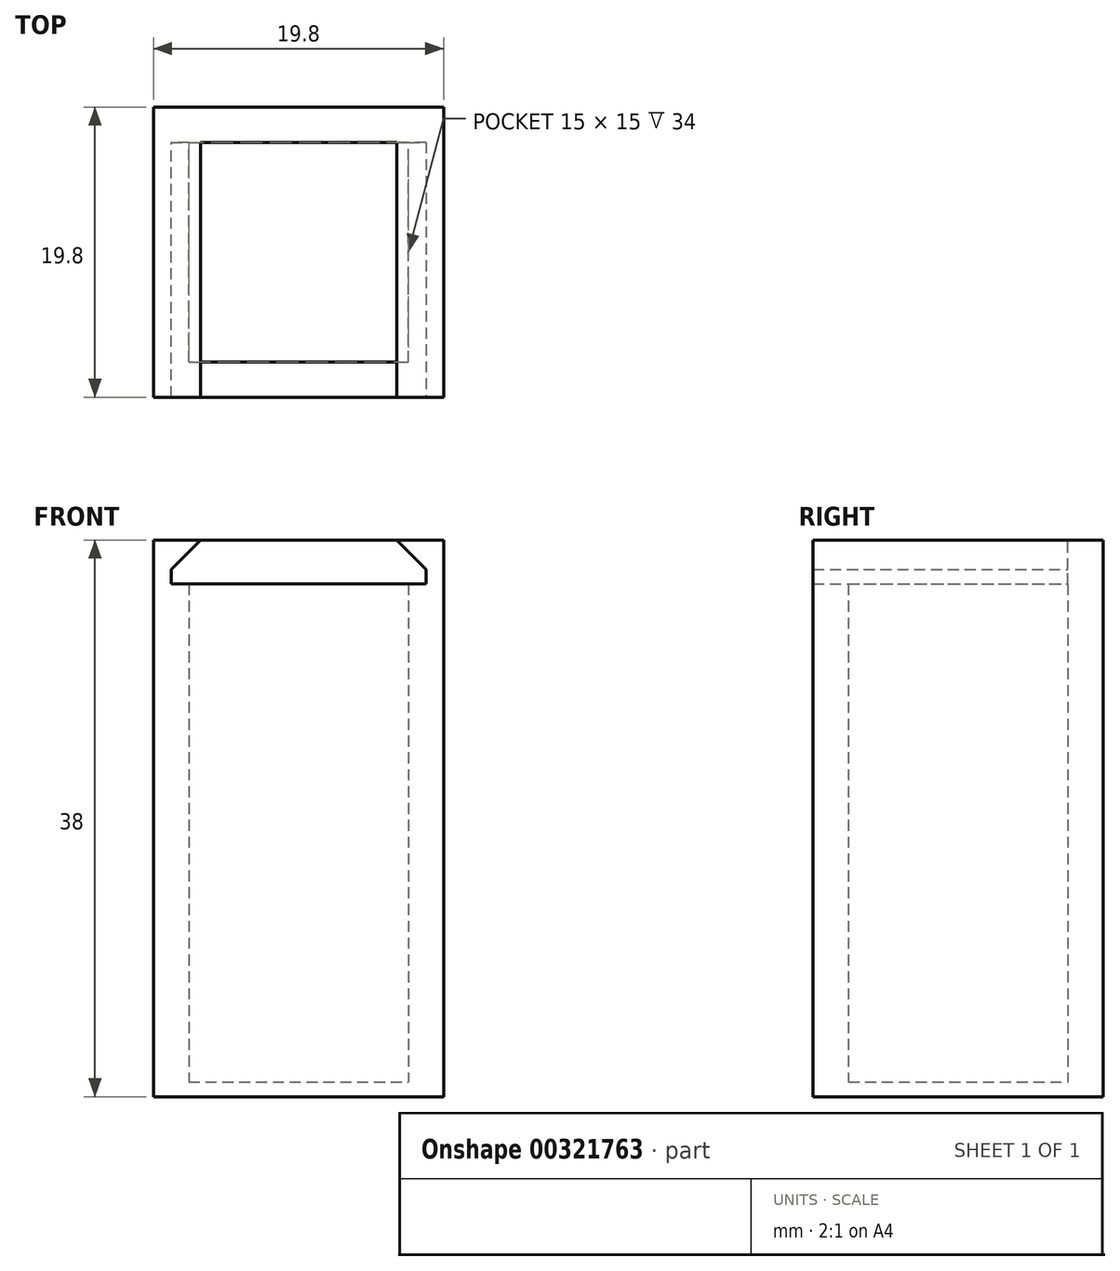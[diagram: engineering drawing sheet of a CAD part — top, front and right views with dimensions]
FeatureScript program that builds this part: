
annotation { "Feature Type Name" : "Feature", "Feature Type Description" : "" }
export const myFeature = defineFeature(function(context is Context, id is Id, definition is map)
    precondition{}
    {
        {
            var Q0;
            Q0=qCreatedBy(makeId("Top.planeOp"),FACE);
            var sketch = newSketch(context, id + "F0", { "sketchPlane" : qUnion([Q0])});
            skLineSegment(sketch, "E0.bottom", {"start": v(-7.5, -7.5) * mm, "end": v(7.5, -7.5) * mm});
            skLineSegment(sketch, "E0.top", {"start": v(-7.5, 7.5) * mm, "end": v(7.5, 7.5) * mm});
            skLineSegment(sketch, "E0.left", {"start": v(-7.5, -7.5) * mm, "end": v(-7.5, 7.5) * mm});
            skLineSegment(sketch, "E0.right", {"start": v(7.5, -7.5) * mm, "end": v(7.5, 7.5) * mm});
            skLineSegment(sketch, "E1", {"start": v(-7.5, 7.5) * mm, "end": v(-7.5, 9.9) * mm});
            skLineSegment(sketch, "E2", {"start": v(-7.5, 9.9) * mm, "end": v(-9.9, 9.9) * mm});
            skLineSegment(sketch, "E3", {"start": v(7.5, -7.5) * mm, "end": v(9.9, -7.5) * mm});
            skLineSegment(sketch, "E4", {"start": v(9.9, -7.5) * mm, "end": v(9.9, -9.9) * mm});
            skLineSegment(sketch, "E5", {"start": v(-7.5, 0) * mm, "end": v(0, 0) * mm});
            skLineSegment(sketch, "E6", {"start": v(0, 0) * mm, "end": v(0, -7.5) * mm});
            skLineSegment(sketch, "E7.bottom", {"start": v(-9.9, 9.9) * mm, "end": v(9.9, 9.9) * mm});
            skLineSegment(sketch, "E7.top", {"start": v(-9.9, -9.9) * mm, "end": v(9.9, -9.9) * mm});
            skLineSegment(sketch, "E7.left", {"start": v(-9.9, 9.9) * mm, "end": v(-9.9, -9.9) * mm});
            skLineSegment(sketch, "E7.right", {"start": v(9.9, 9.9) * mm, "end": v(9.9, -9.9) * mm});
            skSolve(sketch);
        }
        {
            var Q0;
            {var subQ0=sQuery(id+"F0.wireOp",EDGE,"E1");Q0=makeQuery(id+"F0.imprint","IMPRINT",FACE,{"disambiguationData":[TD([[makeQuery(id+"F0.imprint","IMPRINT",EDGE,{"derivedFrom":subQ0}),1.0]])]});}
            var Q1;
            Q1=makeQuery(id+"F0.imprint","IMPRINT",FACE,{"disambiguationData":[TD([[makeQuery(id+"F0.imprint","IMPRINT",EDGE,{"derivedFrom":sQuery(id+"F0.wireOp",EDGE,"E0.top")}),1.0]])]});
            extrude(context, id + "F1", {"entities" : qUnion([Q0, Q1]), "depth" : 25 * mm});
        }
        {
            var Q0;
            Q0=makeQuery(id+"F1.opExtrude","CAP_FACE",FACE,{"disambiguationData":[OSD([sQuery(id+"F0.wireOp",EDGE,"E0.bottom"),sQuery(id+"F0.wireOp",EDGE,"E0.top"),sQuery(id+"F0.wireOp",EDGE,"E0.left"),sQuery(id+"F0.wireOp",EDGE,"E0.right"),sQuery(id+"F0.wireOp",EDGE,"E7.bottom"),sQuery(id+"F0.wireOp",EDGE,"E7.top"),sQuery(id+"F0.wireOp",EDGE,"E7.left"),sQuery(id+"F0.wireOp",EDGE,"E7.right")])],"isStart":true});
            var sketch = newSketch(context, id + "F2", { "sketchPlane" : qUnion([Q0])});
            skLineSegment(sketch, "E8.bottom", {"start": v(-9.9, 9.9) * mm, "end": v(9.9, 9.9) * mm});
            skLineSegment(sketch, "E8.top", {"start": v(-9.9, -9.9) * mm, "end": v(9.9, -9.9) * mm});
            skLineSegment(sketch, "E8.left", {"start": v(-9.9, 9.9) * mm, "end": v(-9.9, -9.9) * mm});
            skLineSegment(sketch, "E8.right", {"start": v(9.9, 9.9) * mm, "end": v(9.9, -9.9) * mm});
            skSolve(sketch);
        }
        {
            var Q0;
            Q0=qSketchRegion(id+"F2",true);
            extrude(context, id + "F3", {"entities" : qUnion([Q0]), "operationType" : NewBodyOperationType.ADD, "depth" : 1 * mm});
        }
        {
            var Q0;
            Q0=makeQuery(id+"F1.opExtrude","CAP_FACE",FACE,{"disambiguationData":[OSD([sQuery(id+"F0.wireOp",EDGE,"E0.bottom"),sQuery(id+"F0.wireOp",EDGE,"E0.top"),sQuery(id+"F0.wireOp",EDGE,"E0.left"),sQuery(id+"F0.wireOp",EDGE,"E0.right"),sQuery(id+"F0.wireOp",EDGE,"E7.bottom"),sQuery(id+"F0.wireOp",EDGE,"E7.top"),sQuery(id+"F0.wireOp",EDGE,"E7.left"),sQuery(id+"F0.wireOp",EDGE,"E7.right")])],"isStart":false});
            var sketch = newSketch(context, id + "F4", { "sketchPlane" : qUnion([Q0])});
            skLineSegment(sketch, "E9", {"start": v(-9.9, 0) * mm, "end": v(-8.7, 0) * mm});
            skPoint(sketch, "E9.endSnap0", {"position": v(-7.5, 0) * mm});
            skLineSegment(sketch, "E10", {"start": v(9.9, 0) * mm, "end": v(8.7, 0) * mm});
            skLineSegment(sketch, "E11", {"start": v(-8.7, 0) * mm, "end": v(-8.7, -10.6) * mm});
            skLineSegment(sketch, "E12", {"start": v(8.7, 0) * mm, "end": v(8.7, -11.22) * mm});
            skLineSegment(sketch, "E13", {"start": v(-8.7, -10.6) * mm, "end": v(8.7, -10.6) * mm});
            skLineSegment(sketch, "E14", {"start": v(-7.5, 7.5) * mm, "end": v(-9.9, 7.5) * mm});
            skLineSegment(sketch, "E15", {"start": v(7.5, 7.5) * mm, "end": v(9.9, 7.5) * mm});
            skLineSegment(sketch, "E16", {"start": v(-8.7, 0) * mm, "end": v(-8.7, 7.5) * mm});
            skLineSegment(sketch, "E17", {"start": v(8.7, 0) * mm, "end": v(8.7, 7.5) * mm});
            skLineSegment(sketch, "E18", {"start": v(-7.5, 7.5) * mm, "end": v(7.5, 7.5) * mm});
            skSolve(sketch);
        }
        {
            var Q0;
            {var subQ11=sQuery(id+"F4.wireOp",EDGE,"E16");Q0=makeQuery(id+"F4.imprint","IMPRINT",FACE,{"disambiguationData":[TD([[makeQuery(id+"F4.imprint","IMPRINT",EDGE,{"derivedFrom":subQ11}),-1.0]])]});}
            extrude(context, id + "F5", {"entities" : qUnion([Q0]), "operationType" : NewBodyOperationType.REMOVE, "oppositeDirection" : true, "depth" : 2 * mm});
        }
        {
            var Q0;
            Q0=makeQuery(id+"F3.boolean.opBoolean","MERGE",FACE,{"derivedFrom":[makeQuery(id+"F1.opExtrude","SWEPT_FACE",FACE,{"disambiguationData":[OSD([sQuery(id+"F0.wireOp",EDGE,"E7.top")])]}),makeQuery(id+"F3.opExtrude","SWEPT_FACE",FACE,{"disambiguationData":[OSD([sQuery(id+"F2.wireOp",EDGE,"E8.bottom")])]})]});
            var sketch = newSketch(context, id + "F6", { "sketchPlane" : qUnion([Q0])});
            skLineSegment(sketch, "E19", {"start": v(-9.9, 25) * mm, "end": v(-9.9, 27) * mm});
            skLineSegment(sketch, "E20", {"start": v(9.9, 25) * mm, "end": v(9.9, 27) * mm});
            skLineSegment(sketch, "E21", {"start": v(-9.9, 27) * mm, "end": v(9.9, 27) * mm});
            skLineSegment(sketch, "E22", {"start": v(-8.7, 25) * mm, "end": v(-6.7, 27) * mm});
            skLineSegment(sketch, "E23", {"start": v(8.7, 25) * mm, "end": v(6.7, 27) * mm});
            skLineSegment(sketch, "E24", {"start": v(-9.9, 25) * mm, "end": v(-8.7, 25) * mm});
            skLineSegment(sketch, "E25", {"start": v(8.7, 25) * mm, "end": v(9.9, 25) * mm});
            skSolve(sketch);
        }
        {
            var Q0;
            Q0=makeQuery(id+"F5.boolean.opBoolean","COPY",FACE,{"derivedFrom":makeQuery(id+"F5.opExtrude","CAP_FACE",FACE,{"disambiguationData":[OSD([sQuery(id+"F0.wireOp",EDGE,"E0.bottom"),sQuery(id+"F0.wireOp",EDGE,"E0.left"),sQuery(id+"F0.wireOp",EDGE,"E0.right"),sQuery(id+"F0.wireOp",EDGE,"E7.top"),sQuery(id+"F4.wireOp",EDGE,"E11"),sQuery(id+"F4.wireOp",EDGE,"E12"),sQuery(id+"F4.wireOp",EDGE,"E14"),sQuery(id+"F4.wireOp",EDGE,"E15"),sQuery(id+"F4.wireOp",EDGE,"E16"),sQuery(id+"F4.wireOp",EDGE,"E17")])],"isStart":false})});
            extrude(context, id + "F7", {"entities" : qUnion([Q0]), "operationType" : NewBodyOperationType.ADD, "depth" : 1 * mm});
        }
        {
            var Q0;
            {var subQ0=sQuery(id+"F6.wireOp",EDGE,"E19");Q0=makeQuery(id+"F6.imprint","IMPRINT",FACE,{"disambiguationData":[TD([[makeQuery(id+"F6.imprint","IMPRINT",EDGE,{"derivedFrom":subQ0}),-1.0]])]});}
            var Q1;
            {var subQ0=sQuery(id+"F6.wireOp",EDGE,"E20");Q1=makeQuery(id+"F6.imprint","IMPRINT",FACE,{"disambiguationData":[TD([[makeQuery(id+"F6.imprint","IMPRINT",EDGE,{"derivedFrom":subQ0}),1.0]])]});}
            var Q2;
            Q2=makeQuery(id+"F3.boolean.opBoolean","MERGE",FACE,{"derivedFrom":[makeQuery(id+"F1.opExtrude","SWEPT_FACE",FACE,{"disambiguationData":[OSD([sQuery(id+"F0.wireOp",EDGE,"E7.bottom")])]}),makeQuery(id+"F3.opExtrude","SWEPT_FACE",FACE,{"disambiguationData":[OSD([sQuery(id+"F2.wireOp",EDGE,"E8.top")])]})]});
            extrude(context, id + "F8", {"entities" : qUnion([Q0, Q1]), "operationType" : NewBodyOperationType.ADD, "endBound" : BoundingType.UP_TO_SURFACE, "oppositeDirection" : true, "endBoundEntityFace" : qUnion([Q2]), "depth" : 25 * mm});
        }
        {
            var Q0;
            {var subQ0=sQuery(id+"F6.wireOp",EDGE,"E21");var subQ1=sQuery(id+"F2.wireOp",EDGE,"E8.top");var subQ2=sQuery(id+"F0.wireOp",EDGE,"E7.bottom");Q0=makeQuery(id+"F8.boolean.opBoolean","MERGE",FACE,{"derivedFrom":[makeQuery(id+"F3.boolean.opBoolean","MERGE",FACE,{"derivedFrom":[makeQuery(id+"F1.opExtrude","SWEPT_FACE",FACE,{"disambiguationData":[OSD([subQ2])]}),makeQuery(id+"F3.opExtrude","SWEPT_FACE",FACE,{"disambiguationData":[OSD([subQ1])]})]}),makeQuery(id+"F8.opExtrude","CAP_FACE",FACE,{"disambiguationData":[OSD([subQ2,subQ1]),ownerDisambiguation([makeQuery(id+"F8.opExtrude","SWEPT_BODY",BODY,{"disambiguationData":[OSD([sQuery(id+"F6.wireOp",EDGE,"E19"),subQ0,sQuery(id+"F6.wireOp",EDGE,"E22"),sQuery(id+"F6.wireOp",EDGE,"E24")])]})])],"isStart":false}),makeQuery(id+"F8.opExtrude","CAP_FACE",FACE,{"disambiguationData":[OSD([subQ2,subQ1]),ownerDisambiguation([makeQuery(id+"F8.opExtrude","SWEPT_BODY",BODY,{"disambiguationData":[OSD([sQuery(id+"F6.wireOp",EDGE,"E20"),subQ0,sQuery(id+"F6.wireOp",EDGE,"E23"),sQuery(id+"F6.wireOp",EDGE,"E25")])]})])],"isStart":false})]});}
            var sketch = newSketch(context, id + "F9", { "sketchPlane" : qUnion([Q0])});
            skLineSegment(sketch, "E26", {"start": v(-6.7, 27) * mm, "end": v(-6.7, 25) * mm});
            skLineSegment(sketch, "E27", {"start": v(-6.7, 25) * mm, "end": v(-8.7, 25) * mm});
            skLineSegment(sketch, "E28", {"start": v(-8.7, 25) * mm, "end": v(-6.7, 27) * mm});
            skLineSegment(sketch, "E29", {"start": v(6.7, 27) * mm, "end": v(6.7, 25) * mm});
            skLineSegment(sketch, "E30", {"start": v(6.7, 25) * mm, "end": v(8.7, 25) * mm});
            skLineSegment(sketch, "E31", {"start": v(8.7, 25) * mm, "end": v(6.7, 27) * mm});
            skSolve(sketch);
        }
        {
            var Q0;
            Q0=makeQuery(id+"F9.imprint","IMPRINT",FACE,{"disambiguationData":[TD([[makeQuery(id+"F9.imprint","IMPRINT",EDGE,{"derivedFrom":sQuery(id+"F9.wireOp",EDGE,"E26")}),-1.0]])]});
            var Q1;
            Q1=makeQuery(id+"F9.imprint","IMPRINT",FACE,{"disambiguationData":[TD([[makeQuery(id+"F9.imprint","IMPRINT",EDGE,{"derivedFrom":sQuery(id+"F9.wireOp",EDGE,"E29")}),1.0]])]});
            var Q2;
            Q2=makeQuery(id+"F5.boolean.opBoolean","MERGE",FACE,{"derivedFrom":[makeQuery(id+"F1.opExtrude","SWEPT_FACE",FACE,{"disambiguationData":[OSD([sQuery(id+"F0.wireOp",EDGE,"E0.top")])]}),makeQuery(id+"F5.opExtrude","SWEPT_FACE",FACE,{"disambiguationData":[OSD([sQuery(id+"F4.wireOp",EDGE,"E14")])]}),makeQuery(id+"F5.opExtrude","SWEPT_FACE",FACE,{"disambiguationData":[OSD([sQuery(id+"F4.wireOp",EDGE,"E15")])]})]});
            extrude(context, id + "F10", {"entities" : qUnion([Q0, Q1]), "operationType" : NewBodyOperationType.ADD, "endBound" : BoundingType.UP_TO_SURFACE, "oppositeDirection" : true, "endBoundEntityFace" : qUnion([Q2]), "depth" : 25 * mm});
        }
        {
            var Q0;
            Q0=makeQuery(id+"F1.opExtrude","CAP_FACE",FACE,{"disambiguationData":[OSD([sQuery(id+"F0.wireOp",EDGE,"E0.bottom"),sQuery(id+"F0.wireOp",EDGE,"E0.top"),sQuery(id+"F0.wireOp",EDGE,"E0.left"),sQuery(id+"F0.wireOp",EDGE,"E0.right"),sQuery(id+"F0.wireOp",EDGE,"E7.bottom"),sQuery(id+"F0.wireOp",EDGE,"E7.top"),sQuery(id+"F0.wireOp",EDGE,"E7.left"),sQuery(id+"F0.wireOp",EDGE,"E7.right")])],"isStart":false});
            var Q1;
            {var subQ0=sQuery(id+"F6.wireOp",EDGE,"E21");Q1=makeQuery(id+"F8.opExtrude","SWEPT_FACE",FACE,{"disambiguationData":[OSD([subQ0]),TDD([makeQuery(id+"F6.imprint","IMPRINT",EDGE,{"disambiguationData":[TD([[makeQuery(id+"F6.imprint","INTERSECT",VERTEX,{"derivedFrom":[sQuery(id+"F6.wireOp",EDGE,"E20"),subQ0]}),1.0]])],"derivedFrom":subQ0})])]});}
            extrude(context, id + "F11", {"entities" : qUnion([Q0]), "operationType" : NewBodyOperationType.ADD, "endBound" : BoundingType.UP_TO_SURFACE, "endBoundEntityFace" : qUnion([Q1]), "depth" : 25 * mm});
        }
        {
            var Q0;
            {var subQ0=sQuery(id+"F6.wireOp",EDGE,"E21");var subQ1=sQuery(id+"F0.wireOp",EDGE,"E7.top");Q0=makeQuery(id+"F8.boolean.opBoolean","MERGE",FACE,{"derivedFrom":[makeQuery(id+"F7.boolean.opBoolean","MERGE",FACE,{"derivedFrom":[makeQuery(id+"F3.boolean.opBoolean","MERGE",FACE,{"derivedFrom":[makeQuery(id+"F1.opExtrude","SWEPT_FACE",FACE,{"disambiguationData":[OSD([subQ1])]}),makeQuery(id+"F3.opExtrude","SWEPT_FACE",FACE,{"disambiguationData":[OSD([sQuery(id+"F2.wireOp",EDGE,"E8.bottom")])]})]}),makeQuery(id+"F7.opExtrude","SWEPT_FACE",FACE,{"disambiguationData":[OSD([subQ1])]})]}),makeQuery(id+"F8.opExtrude","CAP_FACE",FACE,{"disambiguationData":[OSD([sQuery(id+"F6.wireOp",EDGE,"E19"),subQ0,sQuery(id+"F6.wireOp",EDGE,"E22"),sQuery(id+"F6.wireOp",EDGE,"E24")])],"isStart":true}),makeQuery(id+"F8.opExtrude","CAP_FACE",FACE,{"disambiguationData":[OSD([sQuery(id+"F6.wireOp",EDGE,"E20"),subQ0,sQuery(id+"F6.wireOp",EDGE,"E23"),sQuery(id+"F6.wireOp",EDGE,"E25")])],"isStart":true})]});}
            var sketch = newSketch(context, id + "F12", { "sketchPlane" : qUnion([Q0])});
            skLineSegment(sketch, "E32.0", {"start": v(-8.6, 24.1) * mm, "end": v(-8.6, 24.96) * mm});
            skLineSegment(sketch, "E33.0", {"start": v(-8.6, 24.96) * mm, "end": v(-6.63, 26.93) * mm});
            skLineSegment(sketch, "E34.0", {"start": v(-8.6, 24.1) * mm, "end": v(8.6, 24.1) * mm});
            skLineSegment(sketch, "E35.0", {"start": v(8.6, 24.1) * mm, "end": v(8.6, 24.96) * mm});
            skLineSegment(sketch, "E36.0", {"start": v(8.6, 24.96) * mm, "end": v(6.63, 26.93) * mm});
            skLineSegment(sketch, "E37", {"start": v(-6.63, 26.93) * mm, "end": v(6.63, 26.93) * mm});
            skSolve(sketch);
        }
        {
            var Q0;
            Q0=makeQuery(id+"F12.imprint","IMPRINT",FACE,{"disambiguationData":[TD([[makeQuery(id+"F12.imprint","IMPRINT",EDGE,{"derivedFrom":sQuery(id+"F12.wireOp",EDGE,"E32.0")}),-1.0]])]});
            var Q1;
            {var subQ0=sQuery(id+"F4.wireOp",EDGE,"E15");var subQ1=sQuery(id+"F4.wireOp",EDGE,"E14");var subQ2=sQuery(id+"F0.wireOp",EDGE,"E0.top");Q1=makeQuery(id+"F11.boolean.opBoolean","MERGE",FACE,{"derivedFrom":[makeQuery(id+"F10.boolean.opBoolean","MERGE",FACE,{"derivedFrom":[makeQuery(id+"F5.boolean.opBoolean","MERGE",FACE,{"derivedFrom":[makeQuery(id+"F1.opExtrude","SWEPT_FACE",FACE,{"disambiguationData":[OSD([subQ2])]}),makeQuery(id+"F5.opExtrude","SWEPT_FACE",FACE,{"disambiguationData":[OSD([subQ1])]}),makeQuery(id+"F5.opExtrude","SWEPT_FACE",FACE,{"disambiguationData":[OSD([subQ0])]})]}),makeQuery(id+"F10.opExtrude","CAP_FACE",FACE,{"disambiguationData":[OSD([subQ2,subQ1,subQ0]),ownerDisambiguation([makeQuery(id+"F10.opExtrude","SWEPT_BODY",BODY,{"disambiguationData":[OSD([sQuery(id+"F9.wireOp",EDGE,"E26"),sQuery(id+"F9.wireOp",EDGE,"E27"),sQuery(id+"F9.wireOp",EDGE,"E28")])]})])],"isStart":false}),makeQuery(id+"F10.opExtrude","CAP_FACE",FACE,{"disambiguationData":[OSD([subQ2,subQ1,subQ0]),ownerDisambiguation([makeQuery(id+"F10.opExtrude","SWEPT_BODY",BODY,{"disambiguationData":[OSD([sQuery(id+"F9.wireOp",EDGE,"E29"),sQuery(id+"F9.wireOp",EDGE,"E30"),sQuery(id+"F9.wireOp",EDGE,"E31")])]})])],"isStart":false})]}),makeQuery(id+"F11.opExtrude","SWEPT_FACE",FACE,{"disambiguationData":[OSD([subQ2,subQ1,subQ0])]})]});}
            extrude(context, id + "F13", {"entities" : qUnion([Q0]), "endBound" : BoundingType.UP_TO_SURFACE, "oppositeDirection" : true, "endBoundEntityFace" : qUnion([Q1]), "depth" : 25 * mm});
        }
        {
            var Q0;
            Q0=makeQuery(id+"F13.opExtrude","SWEPT_FACE",FACE,{"disambiguationData":[OSD([sQuery(id+"F12.wireOp",EDGE,"E37")])]});
            var sketch = newSketch(context, id + "F14", { "sketchPlane" : qUnion([Q0])});
            skText(sketch, "E38", { "text": "0.4", "fontName": "OpenSans-Regular.ttf"});
            const initialGuessF14  = {"E38": [-0.00317, 0.00541, 0, -1, 0.00637]};
            skSetInitialGuess(sketch, initialGuessF14);
            skSolve(sketch);
        }
        {
            var Q0;
            Q0=qSketchRegion(id+"F14",true);
            extrude(context, id + "F15", {"entities" : qUnion([Q0]), "operationType" : NewBodyOperationType.REMOVE, "oppositeDirection" : true, "depth" : 2 * mm});
        }
        {
            var Q0;
            Q0=makeQuery(id+"F15.boolean.opBoolean","COPY",FACE,{"derivedFrom":makeQuery(id+"F15.opExtrude","CAP_FACE",FACE,{"disambiguationData":[OSD([sQuery(id+"F14.wireOp",EDGE,"E38.sketch_text.stroke-0"),sQuery(id+"F14.wireOp",EDGE,"E38.sketch_text.stroke-1"),sQuery(id+"F14.wireOp",EDGE,"E38.sketch_text.stroke-2"),sQuery(id+"F14.wireOp",EDGE,"E38.sketch_text.stroke-3"),sQuery(id+"F14.wireOp",EDGE,"E38.sketch_text.stroke-4"),sQuery(id+"F14.wireOp",EDGE,"E38.sketch_text.stroke-5"),sQuery(id+"F14.wireOp",EDGE,"E38.sketch_text.stroke-6"),sQuery(id+"F14.wireOp",EDGE,"E38.sketch_text.stroke-7"),sQuery(id+"F14.wireOp",EDGE,"E38.sketch_text.stroke-8"),sQuery(id+"F14.wireOp",EDGE,"E38.sketch_text.stroke-9"),sQuery(id+"F14.wireOp",EDGE,"E38.sketch_text.stroke-10"),sQuery(id+"F14.wireOp",EDGE,"E38.sketch_text.stroke-11"),sQuery(id+"F14.wireOp",EDGE,"E38.sketch_text.stroke-12"),sQuery(id+"F14.wireOp",EDGE,"E38.sketch_text.stroke-13"),sQuery(id+"F14.wireOp",EDGE,"E38.sketch_text.stroke-14"),sQuery(id+"F14.wireOp",EDGE,"E38.sketch_text.stroke-15")])],"isStart":false})});
            var Q1;
            Q1=makeQuery(id+"F15.boolean.opBoolean","COPY",FACE,{"derivedFrom":makeQuery(id+"F15.opExtrude","CAP_FACE",FACE,{"disambiguationData":[OSD([sQuery(id+"F14.wireOp",EDGE,"E38.sketch_text.stroke-16"),sQuery(id+"F14.wireOp",EDGE,"E38.sketch_text.stroke-17"),sQuery(id+"F14.wireOp",EDGE,"E38.sketch_text.stroke-18"),sQuery(id+"F14.wireOp",EDGE,"E38.sketch_text.stroke-19"),sQuery(id+"F14.wireOp",EDGE,"E38.sketch_text.stroke-20"),sQuery(id+"F14.wireOp",EDGE,"E38.sketch_text.stroke-21"),sQuery(id+"F14.wireOp",EDGE,"E38.sketch_text.stroke-22"),sQuery(id+"F14.wireOp",EDGE,"E38.sketch_text.stroke-23")])],"isStart":false})});
            var Q2;
            Q2=makeQuery(id+"F15.boolean.opBoolean","COPY",FACE,{"derivedFrom":makeQuery(id+"F15.opExtrude","CAP_FACE",FACE,{"disambiguationData":[OSD([sQuery(id+"F14.wireOp",EDGE,"E38.sketch_text.stroke-24"),sQuery(id+"F14.wireOp",EDGE,"E38.sketch_text.stroke-25"),sQuery(id+"F14.wireOp",EDGE,"E38.sketch_text.stroke-26"),sQuery(id+"F14.wireOp",EDGE,"E38.sketch_text.stroke-27"),sQuery(id+"F14.wireOp",EDGE,"E38.sketch_text.stroke-28"),sQuery(id+"F14.wireOp",EDGE,"E38.sketch_text.stroke-29"),sQuery(id+"F14.wireOp",EDGE,"E38.sketch_text.stroke-30"),sQuery(id+"F14.wireOp",EDGE,"E38.sketch_text.stroke-31"),sQuery(id+"F14.wireOp",EDGE,"E38.sketch_text.stroke-32"),sQuery(id+"F14.wireOp",EDGE,"E38.sketch_text.stroke-33"),sQuery(id+"F14.wireOp",EDGE,"E38.sketch_text.stroke-34"),sQuery(id+"F14.wireOp",EDGE,"E38.sketch_text.stroke-35"),sQuery(id+"F14.wireOp",EDGE,"E38.sketch_text.stroke-36"),sQuery(id+"F14.wireOp",EDGE,"E38.sketch_text.stroke-37"),sQuery(id+"F14.wireOp",EDGE,"E38.sketch_text.stroke-38"),sQuery(id+"F14.wireOp",EDGE,"E38.sketch_text.stroke-39"),sQuery(id+"F14.wireOp",EDGE,"E38.sketch_text.stroke-40")])],"isStart":false})});
            extrude(context, id + "F16", {"entities" : qUnion([Q0, Q1, Q2]), "operationType" : NewBodyOperationType.REMOVE, "oppositeDirection" : true, "depth" : 2 * mm});
        }
        {
            var Q0;
            {var subQ1=sQuery(id+"F12.wireOp",EDGE,"E33.0");var subQ2=sQuery(id+"F12.wireOp",EDGE,"E37");Q0=makeQuery(id+"F15.boolean.opBoolean","SPLIT",FACE,{"disambiguationData":[TD([makeQuery(id+"F13.opExtrude","SWEPT_FACE",FACE,{"disambiguationData":[OSD([subQ1])]})])],"derivedFrom":makeQuery(id+"F13.opExtrude","SWEPT_FACE",FACE,{"disambiguationData":[OSD([subQ2])]})});}
            var sketch = newSketch(context, id + "F17", { "sketchPlane" : qUnion([Q0])});
            skLineSegment(sketch, "E39", {"start": v(0, 4.97) * mm, "end": v(0, 4) * mm});
            skLineSegment(sketch, "E40", {"start": v(0, 4) * mm, "end": v(-0.49, 4) * mm});
            skLineSegment(sketch, "E41", {"start": v(-0.49, 4) * mm, "end": v(-0.49, 5.29) * mm});
            skLineSegment(sketch, "E42", {"start": v(-0.49, 5.29) * mm, "end": v(0.54, 5.29) * mm});
            skLineSegment(sketch, "E43", {"start": v(0.54, 5.29) * mm, "end": v(0.54, 4) * mm});
            skLineSegment(sketch, "E44", {"start": v(0.54, 4) * mm, "end": v(0, 4) * mm});
            skLineSegment(sketch, "E45", {"start": v(-0.49, 1.88) * mm, "end": v(0.43, 1.88) * mm});
            skLineSegment(sketch, "E46", {"start": v(0.43, 1.88) * mm, "end": v(0.43, 0.38) * mm});
            skLineSegment(sketch, "E47", {"start": v(0.43, 0.38) * mm, "end": v(-0.49, 0.38) * mm});
            skLineSegment(sketch, "E48", {"start": v(-0.49, 0.38) * mm, "end": v(-0.49, 1.88) * mm});
            skLineSegment(sketch, "E49", {"start": v(-1.72, -5.25) * mm, "end": v(-0.8, -5.25) * mm});
            skLineSegment(sketch, "E50", {"start": v(-0.8, -5.25) * mm, "end": v(-0.8, -4.57) * mm});
            skLineSegment(sketch, "E51", {"start": v(-0.8, -4.57) * mm, "end": v(-2.2, -4.57) * mm});
            skLineSegment(sketch, "E52", {"start": v(-2.2, -4.57) * mm, "end": v(-1.72, -5.25) * mm});
            skSolve(sketch);
        }
        {
            var Q0;
            {var subQ0=sQuery(id+"F17.wireOp",EDGE,"E39");Q0=makeQuery(id+"F17.imprint","IMPRINT",FACE,{"disambiguationData":[TD([[makeQuery(id+"F17.imprint","IMPRINT",EDGE,{"derivedFrom":subQ0}),-1.0]])]});}
            var Q1;
            {var subQ0=sQuery(id+"F17.wireOp",EDGE,"E39");Q1=makeQuery(id+"F17.imprint","IMPRINT",FACE,{"disambiguationData":[TD([[makeQuery(id+"F17.imprint","IMPRINT",EDGE,{"derivedFrom":subQ0}),1.0]])]});}
            var Q2;
            {var subQ6=sQuery(id+"F17.wireOp",EDGE,"E45");Q2=makeQuery(id+"F17.imprint","IMPRINT",FACE,{"disambiguationData":[TD([[makeQuery(id+"F17.imprint","IMPRINT",EDGE,{"derivedFrom":subQ6}),-1.0]])]});}
            var Q3;
            {var subQ0=sQuery(id+"F17.wireOp",EDGE,"E49");Q3=makeQuery(id+"F17.imprint","IMPRINT",FACE,{"disambiguationData":[TD([[makeQuery(id+"F17.imprint","IMPRINT",EDGE,{"derivedFrom":subQ0}),1.0]])]});}
            var Q4;
            {var subQ27=sQuery(id+"F12.wireOp",EDGE,"E32.0");var subQ29=sQuery(id+"F12.wireOp",EDGE,"E34.0");Q4=makeQuery(id+"F16.boolean.opBoolean","SPLIT",FACE,{"disambiguationData":[TD([makeQuery(id+"F13.opExtrude","SWEPT_FACE",FACE,{"disambiguationData":[OSD([subQ27])]})])],"derivedFrom":makeQuery(id+"F13.opExtrude","SWEPT_FACE",FACE,{"disambiguationData":[OSD([subQ29])]})});}
            extrude(context, id + "F18", {"entities" : qUnion([Q0, Q1, Q2, Q3]), "operationType" : NewBodyOperationType.ADD, "endBound" : BoundingType.UP_TO_SURFACE, "oppositeDirection" : true, "endBoundEntityFace" : qUnion([Q4]), "depth" : 3 * mm});
        }
        {
            var Q0;
            Q0=makeQuery(id+"F3.opExtrude","CAP_FACE",FACE,{"disambiguationData":[OSD([sQuery(id+"F2.wireOp",EDGE,"E8.bottom"),sQuery(id+"F2.wireOp",EDGE,"E8.top"),sQuery(id+"F2.wireOp",EDGE,"E8.left"),sQuery(id+"F2.wireOp",EDGE,"E8.right")])],"isStart":false});
            extrude(context, id + "F19", {"entities" : qUnion([Q0]), "operationType" : NewBodyOperationType.ADD, "depth" : 10 * mm});
        }
        {
            var Q0;
            Q0=makeQuery(id+"F3.opExtrude","CAP_FACE",FACE,{"disambiguationData":[OSD([sQuery(id+"F2.wireOp",EDGE,"E8.bottom"),sQuery(id+"F2.wireOp",EDGE,"E8.top"),sQuery(id+"F2.wireOp",EDGE,"E8.left"),sQuery(id+"F2.wireOp",EDGE,"E8.right")])],"isStart":true});
            extrude(context, id + "F20", {"entities" : qUnion([Q0]), "operationType" : NewBodyOperationType.REMOVE, "oppositeDirection" : true, "depth" : 10 * mm});
        }
        {
            var Q0;
            Q0=makeQuery(id+"F16.boolean.opBoolean","SPLIT",BODY,{"disambiguationData":[OD(0.0)],"derivedFrom":makeQuery(id+"F13.opExtrude","SWEPT_BODY",BODY,{"disambiguationData":[OSD([sQuery(id+"F12.wireOp",EDGE,"E32.0"),sQuery(id+"F12.wireOp",EDGE,"E33.0"),sQuery(id+"F12.wireOp",EDGE,"E34.0"),sQuery(id+"F12.wireOp",EDGE,"E35.0"),sQuery(id+"F12.wireOp",EDGE,"E36.0"),sQuery(id+"F12.wireOp",EDGE,"E37")])]})});
            deleteBodies(context, id + "F21", {"entities" : qUnion([Q0])});
        }
    });
